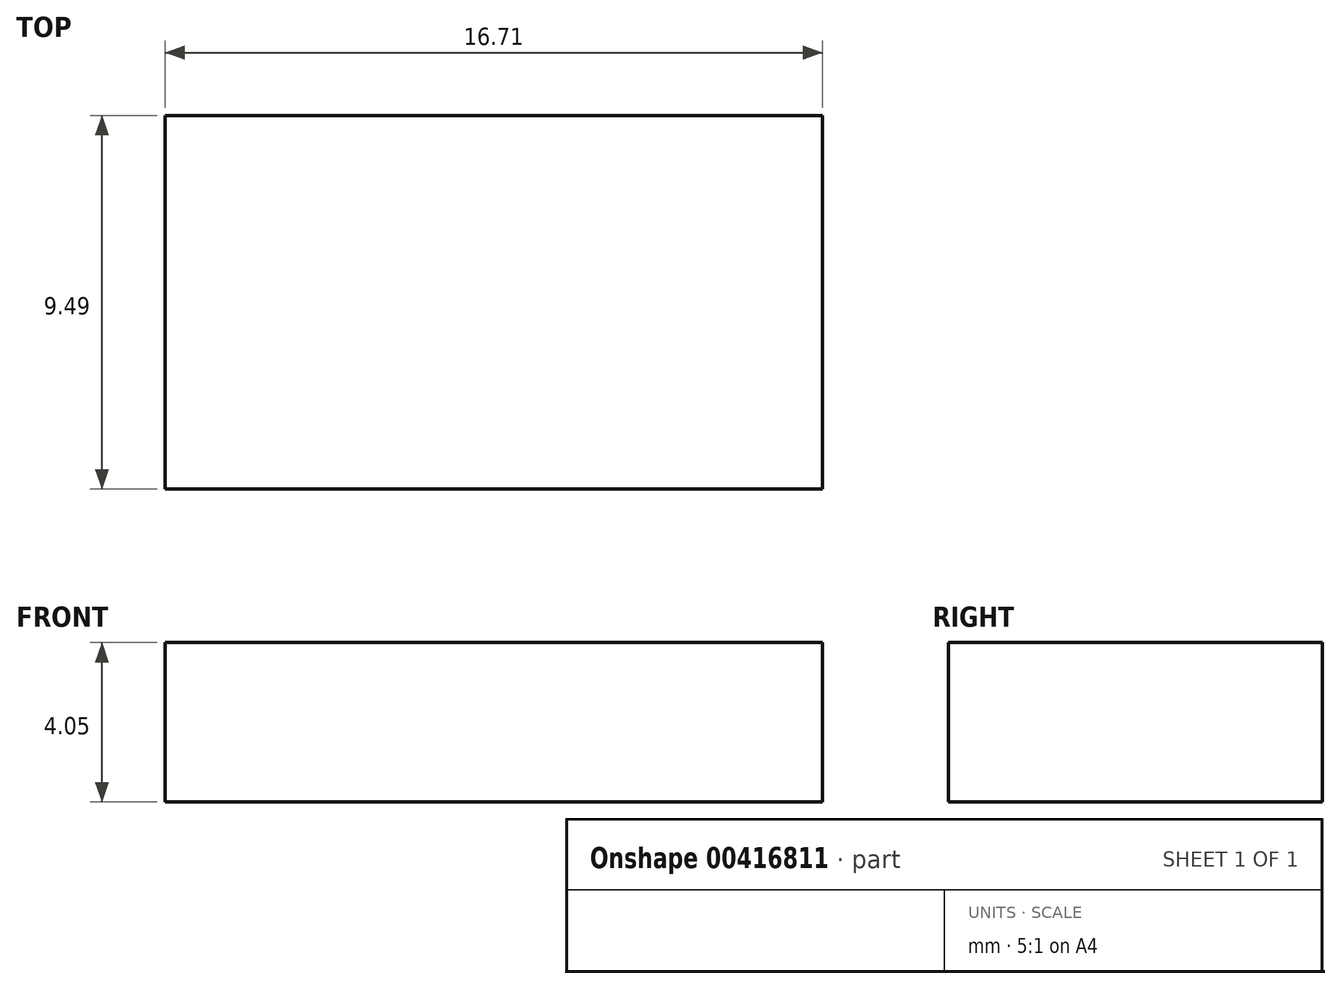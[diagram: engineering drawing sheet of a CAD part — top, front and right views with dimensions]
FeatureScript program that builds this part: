
annotation { "Feature Type Name" : "Feature", "Feature Type Description" : "" }
export const myFeature = defineFeature(function(context is Context, id is Id, definition is map)
    precondition{}
    {
        {
            var Q0;
            Q0=qCreatedBy(makeId("Top.planeOp"),FACE);
            var sketch = newSketch(context, id + "F0", { "sketchPlane" : qUnion([Q0])});
            skLineSegment(sketch, "E0.bottom", {"start": v(0, 0) * mm, "end": v(16.71, 0) * mm});
            skLineSegment(sketch, "E0.top", {"start": v(0, 9.49) * mm, "end": v(16.71, 9.49) * mm});
            skLineSegment(sketch, "E0.left", {"start": v(0, 0) * mm, "end": v(0, 9.49) * mm});
            skLineSegment(sketch, "E0.right", {"start": v(16.71, 0) * mm, "end": v(16.71, 9.49) * mm});
            skSolve(sketch);
        }
        {
            var Q0;
            Q0 = qSketchRegion(id + "F0", true);
            extrude(context, id + "F1", {"entities" : qUnion([Q0]), "depth" : 4.05 * mm, "offsetDistance" : 25.4 * mm});
        }
    });
